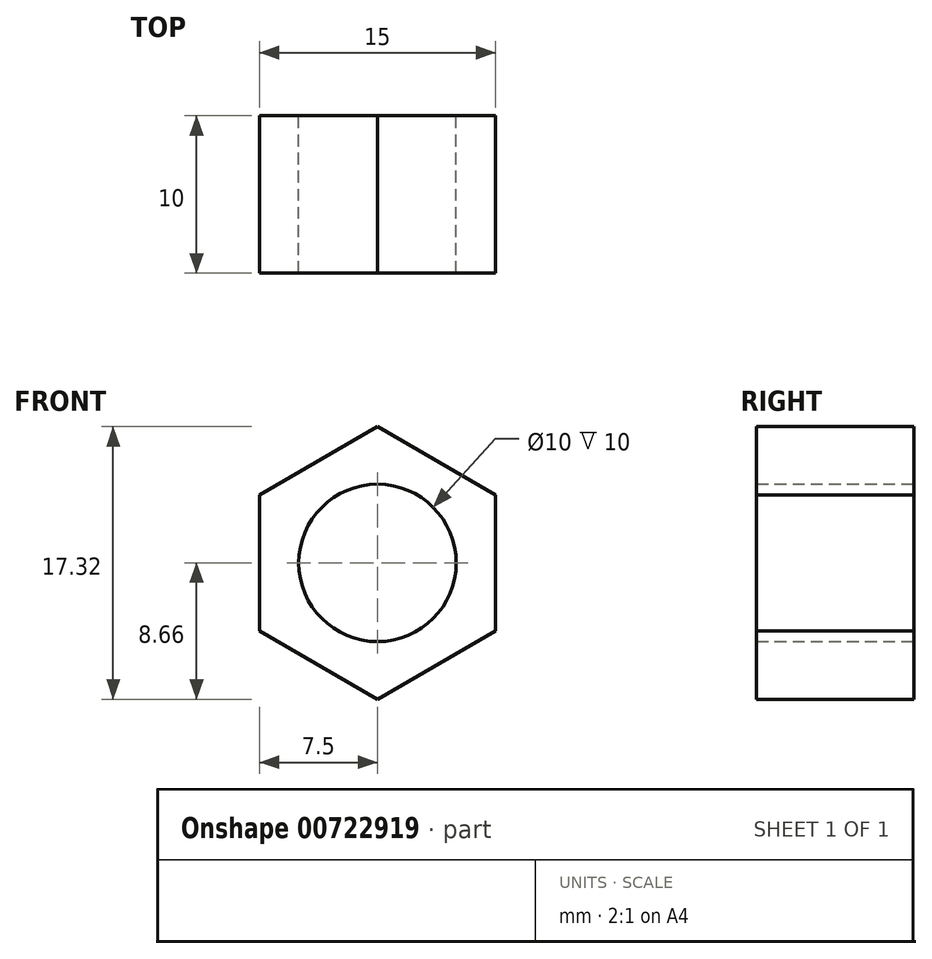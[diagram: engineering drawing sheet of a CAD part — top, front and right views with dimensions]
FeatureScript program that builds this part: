
annotation { "Feature Type Name" : "Feature", "Feature Type Description" : "" }
export const myFeature = defineFeature(function(context is Context, id is Id, definition is map)
    precondition{}
    {
        {
            var Q0;
            Q0=qCreatedBy(makeId("Front.planeOp"),FACE);
            var sketch = newSketch(context, id + "F0", { "sketchPlane" : qUnion([Q0])});
            skCircle(sketch, "E0.cCircle", {"center": v(0, 0) * mm, "radius": 7.5 * mm, "construction": true});
            skLineSegment(sketch, "E0.0", {"start": v(7.5, 4.33) * mm, "end": v(7.5, -4.33) * mm});
            skLineSegment(sketch, "E0.1", {"start": v(7.5, -4.33) * mm, "end": v(0, -8.66) * mm});
            skLineSegment(sketch, "E0.2", {"start": v(0, -8.66) * mm, "end": v(-7.5, -4.33) * mm});
            skLineSegment(sketch, "E0.3", {"start": v(-7.5, -4.33) * mm, "end": v(-7.5, 4.33) * mm});
            skLineSegment(sketch, "E0.4", {"start": v(-7.5, 4.33) * mm, "end": v(0, 8.66) * mm});
            skLineSegment(sketch, "E0.5", {"start": v(0, 8.66) * mm, "end": v(7.5, 4.33) * mm});
            skPoint(sketch, "E0.0.midPoint", {"position": v(7.5, 0) * mm});
            skCircle(sketch, "E1", {"center": v(0, 0) * mm, "radius": 5 * mm});
            skSolve(sketch);
        }
        {
            var Q0;
            Q0=makeQuery(id+"F0.imprint","IMPRINT",FACE,{"disambiguationData":[TD([[makeQuery(id+"F0.imprint","IMPRINT",EDGE,{"derivedFrom":sQuery(id+"F0.wireOp",EDGE,"E0.0")}),-1.0]])]});
            extrude(context, id + "F1", {"entities" : qUnion([Q0]), "depth" : 10 * mm, "offsetDistance" : 25 * mm});
        }
    });
